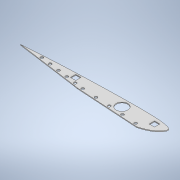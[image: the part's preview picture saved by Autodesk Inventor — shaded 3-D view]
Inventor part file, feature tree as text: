
AUTODESK INVENTOR PART (.ipt)
format: ipt  version: 2021 (Build 250183000, 183)  size: 185,856 bytes
history: native  units: mm
features: extrude x1, sketch x1
ambient origin geometry x8: Origin, YZ Plane, XZ Plane, XY Plane, X Axis, Y Axis, Z Axis, Center Point
bodies: Solid1 (feature_tree)
feature tree (2):
  extrude  "Extrusion1"  Depth=2.0mm
  sketch  "Sketch1"  dims[d0=364.0mm d2=28.5mm d3=18.5mm d12=13.0mm d13=13.0mm d14=13.0mm d15=13.0mm d16=313.0mm d17=313.0mm d44=7.0mm d45=7.0mm d46=7.0mm d47=7.0mm d48=7.0mm d49=47.301625mm d50=7.0mm d52=100.0mm d56=5.5mm d57=96.175852mm d58=24.044mm d59=24.044mm d60=24.044mm d61=24.044mm d62=5.5mm d63=5.5mm d64=7.0mm d65=7.0mm d66=90.0deg d67=7.0mm d68=7.0mm d69=2.0mm d70=0.0mm]
